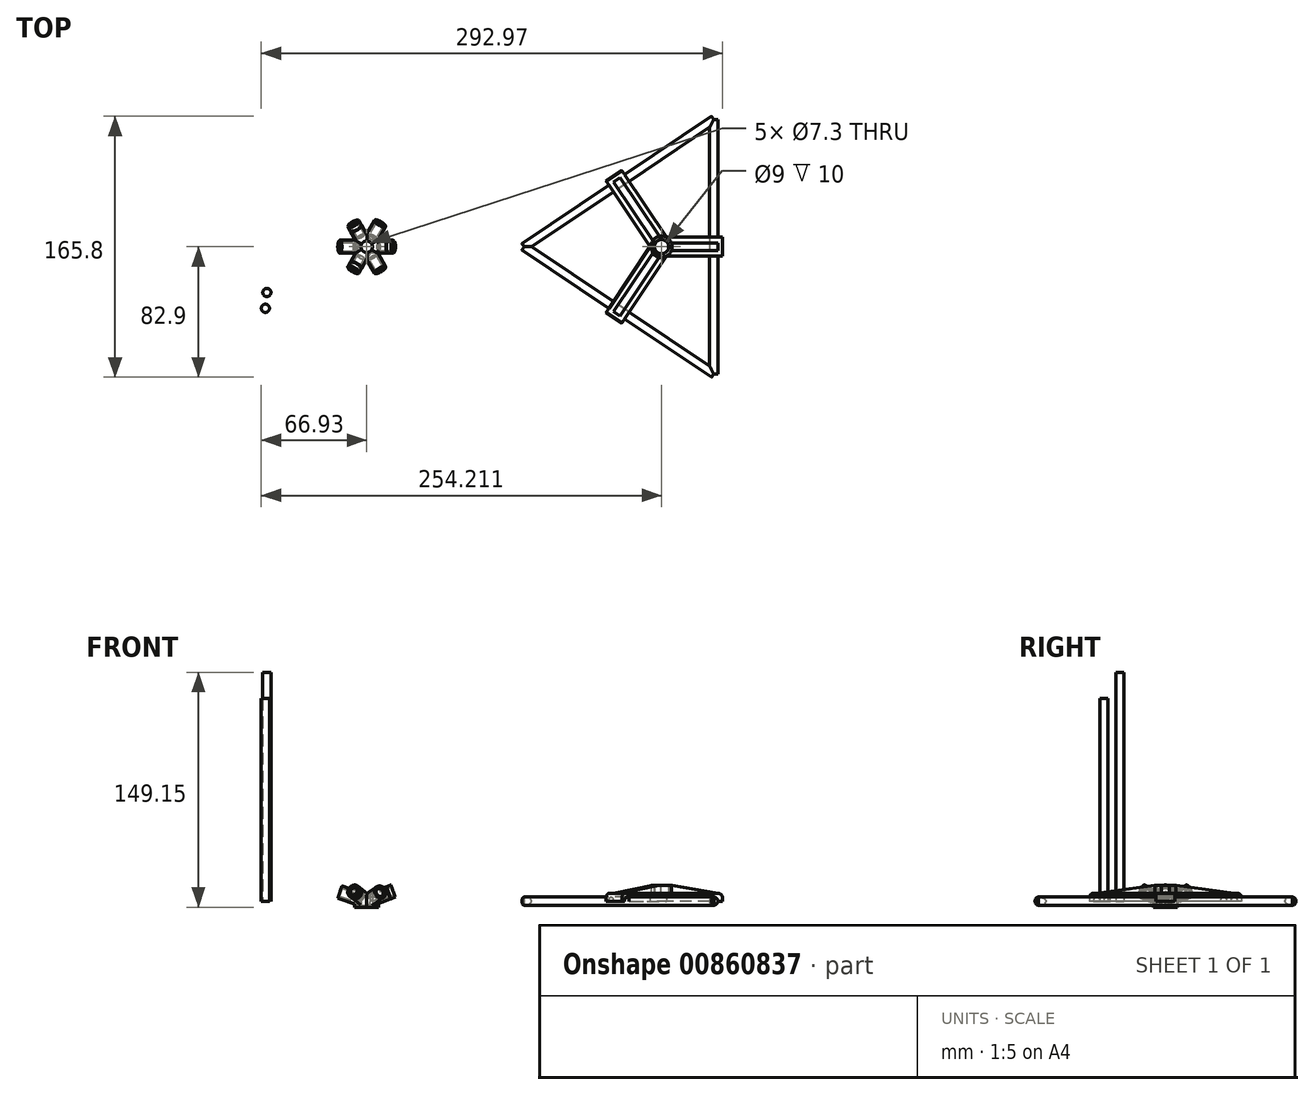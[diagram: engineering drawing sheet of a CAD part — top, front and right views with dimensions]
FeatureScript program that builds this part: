
annotation { "Feature Type Name" : "Feature", "Feature Type Description" : "" }
export const myFeature = defineFeature(function(context is Context, id is Id, definition is map)
    precondition{}
    {
        {
            assignVariable(context, id + "F0", {"name" : "espesor", "anyValue" : 1.5});
        }
        {
            assignVariable(context, id + "F1", {"name" : "longitud", "anyValue" : 18});
        }
        {
            assignVariable(context, id + "F2", {"name" : "relacion", "anyValue" : 1.11});
        }
        {
            assignVariable(context, id + "F3", {"name" : "lvarilla", "anyValue" : 145});
        }
        {
            assignVariable(context, id + "F4", {"name" : "lrecortada", "anyValue" : getVariable(context, 'lvarilla') - 2 * (getVariable(context, 'longitud') * 1.8 / 4)});
        }
        {
            assignVariable(context, id + "F5", {"name" : "lrecortadalarga", "anyValue" : (getVariable(context, 'lvarilla') * getVariable(context, 'relacion') - 2 * (getVariable(context, 'longitud') * 1.8 / 4))});
        }
        {
            var Q0;
            Q0=qCreatedBy(makeId("Front.planeOp"),FACE);
            var sketch = newSketch(context, id + "F6", { "sketchPlane" : qUnion([Q0])});
            skLineSegment(sketch, "E0", {"start": v(0, 0) * mm, "end": v(16.82, 6.42) * mm, "construction": true});
            skLineSegment(sketch, "E1", {"start": v(0, 0) * mm, "end": v(1.46, -3.83) * mm});
            skLineSegment(sketch, "E2", {"start": v(16.82, 6.42) * mm, "end": v(18.28, 2.6) * mm});
            skLineSegment(sketch, "E3", {"start": v(1.46, -3.83) * mm, "end": v(15.1, 1.38) * mm});
            skLineSegment(sketch, "E4", {"start": v(17.74, 4) * mm, "end": v(8.5, 0.46) * mm});
            skLineSegment(sketch, "E5", {"start": v(8.5, 0.46) * mm, "end": v(7.57, 2.9) * mm});
            skLineSegment(sketch, "E6", {"start": v(7.57, 2.9) * mm, "end": v(0, 0) * mm});
            skLineSegment(sketch, "E7", {"start": v(0, 0) * mm, "end": v(0, 41.35) * mm, "construction": true});
            skLineSegment(sketch, "E8", {"start": v(1.46, -3.83) * mm, "end": v(0, -3.83) * mm, "construction": true});
            skLineSegment(sketch, "E9", {"start": v(7.57, 2.9) * mm, "end": v(7.57, -3.83) * mm, "construction": true});
            skLineSegment(sketch, "E10", {"start": v(7.57, -3.83) * mm, "end": v(1.46, -3.83) * mm, "construction": true});
            skLineSegment(sketch, "E11", {"start": v(0, -3.83) * mm, "end": v(7.57, -3.83) * mm});
            skLineSegment(sketch, "E12", {"start": v(7.57, -3.83) * mm, "end": v(7.57, 2.9) * mm});
            skLineSegment(sketch, "E13", {"start": v(0, 2.9) * mm, "end": v(7.57, 2.9) * mm});
            skLineSegment(sketch, "E14", {"start": v(0, 2.9) * mm, "end": v(0, -3.83) * mm});
            skLineSegment(sketch, "E15", {"start": v(15.48, 1.52) * mm, "end": v(15.44, 1.62) * mm});
            skLineSegment(sketch, "E16", {"start": v(15.44, 1.62) * mm, "end": v(15.07, 1.47) * mm});
            skLineSegment(sketch, "E17", {"start": v(15.07, 1.47) * mm, "end": v(15.1, 1.38) * mm});
            skLineSegment(sketch, "E18.trimOffspring", {"start": v(15.48, 1.52) * mm, "end": v(18.28, 2.6) * mm});
            skSolve(sketch);
        }
        {
            var Q0;
            Q0=qCreatedBy(makeId("Front.planeOp"),FACE);
            var sketch = newSketch(context, id + "F7", { "sketchPlane" : qUnion([Q0])});
            skLineSegment(sketch, "E19", {"start": v(0, 0) * mm, "end": v(0, 45.08) * mm, "construction": true});
            skLineSegment(sketch, "E20.MirrorCS", {"start": v(-8.5, 0.13) * mm, "end": v(-7.67, 2.6) * mm});
            skLineSegment(sketch, "E21.MirrorCS", {"start": v(-17.05, 5.77) * mm, "end": v(-18.36, 1.88) * mm});
            skLineSegment(sketch, "E22.MirrorCS", {"start": v(-7.67, 2.6) * mm, "end": v(0, 0) * mm});
            skLineSegment(sketch, "E23.MirrorCS", {"start": v(0, 0) * mm, "end": v(-17.05, 5.77) * mm, "construction": true});
            skLineSegment(sketch, "E24.MirrorCS", {"start": v(0, 2.6) * mm, "end": v(-7.67, 2.6) * mm});
            skLineSegment(sketch, "E25.MirrorCS", {"start": v(-17.88, 3.3) * mm, "end": v(-8.5, 0.13) * mm});
            skLineSegment(sketch, "E26", {"start": v(-18.36, 1.88) * mm, "end": v(-1.31, -3.88) * mm});
            skLineSegment(sketch, "E27", {"start": v(0, 0) * mm, "end": v(-1.31, -3.88) * mm});
            skLineSegment(sketch, "E28", {"start": v(-1.31, -3.88) * mm, "end": v(-7.67, -3.88) * mm});
            skLineSegment(sketch, "E29", {"start": v(-1.31, -3.88) * mm, "end": v(0, -3.88) * mm});
            skLineSegment(sketch, "E30", {"start": v(0, -3.88) * mm, "end": v(0, 2.6) * mm});
            skLineSegment(sketch, "E31", {"start": v(-7.67, 2.6) * mm, "end": v(-7.67, -3.88) * mm});
            skSolve(sketch);
        }
        {
            var Q0;
            {var subQ1=sQuery(id+"F6.wireOp",EDGE,"E4");Q0=makeQuery(id+"F6.imprint","IMPRINT",FACE,{"disambiguationData":[TD([[makeQuery(id+"F6.imprint","IMPRINT",EDGE,{"derivedFrom":subQ1}),1.0]])]});}
            var Q1;
            {var subQ0=sQuery(id+"F6.wireOp",EDGE,"E1");Q1=makeQuery(id+"F6.imprint","IMPRINT",FACE,{"disambiguationData":[TD([[makeQuery(id+"F6.imprint","IMPRINT",EDGE,{"derivedFrom":subQ0}),1.0]])]});}
            var Q2;
            Q2=sQuery(id+"F6.wireOp",EDGE,"E0");
            revolve(context, id + "F8", {"surfaceOperationType" : NewSurfaceOperationType.NEW, "entities" : qUnion([Q0, Q1]), "axis" : qUnion([Q2]), "revolveType" : RevolveType.FULL});
        }
        {
            var Q0;
            {var subQ5=sQuery(id+"F7.wireOp",EDGE,"E20.MirrorCS");Q0=makeQuery(id+"F7.imprint","IMPRINT",FACE,{"disambiguationData":[TD([[makeQuery(id+"F7.imprint","IMPRINT",EDGE,{"derivedFrom":subQ5}),-1.0]])]});}
            var Q1;
            {var subQ0=sQuery(id+"F7.wireOp",EDGE,"E22.MirrorCS");Q1=makeQuery(id+"F7.imprint","IMPRINT",FACE,{"disambiguationData":[TD([[makeQuery(id+"F7.imprint","IMPRINT",EDGE,{"derivedFrom":subQ0}),-1.0]])]});}
            var Q2;
            Q2=sQuery(id+"F7.wireOp",EDGE,"E23.MirrorCS");
            revolve(context, id + "F9", {"surfaceOperationType" : NewSurfaceOperationType.NEW, "entities" : qUnion([Q0, Q1]), "axis" : qUnion([Q2]), "revolveType" : RevolveType.FULL});
        }
        {
            var Q0;
            Q0=makeQuery(id+"F8.opRevolve","SWEPT_BODY",BODY,{"disambiguationData":[OSD([sQuery(id+"F6.wireOp",EDGE,"E1"),sQuery(id+"F6.wireOp",EDGE,"E2"),sQuery(id+"F6.wireOp",EDGE,"E3"),sQuery(id+"F6.wireOp",EDGE,"E4"),sQuery(id+"F6.wireOp",EDGE,"E5"),sQuery(id+"F6.wireOp",EDGE,"E6")])]});
            var Q1;
            Q1=sQuery(id+"F6.wireOp",EDGE,"E7");
            circularPattern(context, id + "F10", {"operationType" : NewBodyOperationType.ADD, "entities" : qUnion([Q0]), "axis" : qUnion([Q1]), "angle" : 360 * degree, "instanceCount" : 3, "equalSpace" : true});
        }
        {
            var Q0;
            Q0=makeQuery(id+"FgpRCOrkwi8NXZ9_2.boolean.opBoolean","SPLIT",BODY,{"disambiguationData":[OD(1.0)],"derivedFrom":makeQuery(id+"F9.opRevolve","SWEPT_BODY",BODY,{"disambiguationData":[OSD([sQuery(id+"F7.wireOp",EDGE,"E20.MirrorCS"),sQuery(id+"F7.wireOp",EDGE,"E21.MirrorCS"),sQuery(id+"F7.wireOp",EDGE,"E22.MirrorCS"),sQuery(id+"F7.wireOp",EDGE,"E25.MirrorCS"),sQuery(id+"F7.wireOp",EDGE,"E26"),sQuery(id+"F7.wireOp",EDGE,"E27")])]})});
            var Q1;
            Q1=sQuery(id+"F7.wireOp",EDGE,"E19");
            circularPattern(context, id + "F11", {"entities" : qUnion([Q0]), "axis" : qUnion([Q1]), "angle" : 360 * degree, "instanceCount" : 3, "equalSpace" : true});
        }
        {
            var Q0;
            {var subQ0=sQuery(id+"F6.wireOp",EDGE,"E1");Q0=makeQuery(id+"F6.imprint","IMPRINT",FACE,{"disambiguationData":[TD([[makeQuery(id+"F6.imprint","IMPRINT",EDGE,{"derivedFrom":subQ0}),-1.0]])]});}
            var Q1;
            {var subQ0=sQuery(id+"F6.wireOp",EDGE,"E1");Q1=makeQuery(id+"F6.imprint","IMPRINT",FACE,{"disambiguationData":[TD([[makeQuery(id+"F6.imprint","IMPRINT",EDGE,{"derivedFrom":subQ0}),1.0]])]});}
            var Q2;
            {var subQ0=sQuery(id+"F6.wireOp",EDGE,"E11");var subQ3=sQuery(id+"F6.wireOp",EDGE,"E12");var subQ5=makeQuery(id+"F6.imprint","INTERSECT",VERTEX,{"derivedFrom":[subQ0,subQ3]});Q2=makeQuery(id+"F6.imprint","IMPRINT",FACE,{"disambiguationData":[TD([[makeQuery(id+"F6.imprint","IMPRINT",EDGE,{"disambiguationData":[TD([[subQ5,-1.0]])],"derivedFrom":subQ3}),1.0]])]});}
            var Q3;
            {var subQ0=sQuery(id+"F6.wireOp",EDGE,"E6");Q3=makeQuery(id+"F6.imprint","IMPRINT",FACE,{"disambiguationData":[TD([[makeQuery(id+"F6.imprint","IMPRINT",EDGE,{"derivedFrom":subQ0}),-1.0]])]});}
            var Q4;
            Q4=sQuery(id+"F6.wireOp",EDGE,"E13");
            var Q5;
            Q5=sQuery(id+"F6.wireOp",EDGE,"E14");
            var Q6;
            Q6=sQuery(id+"F6.wireOp",EDGE,"E7");
            revolve(context, id + "F12", {"surfaceOperationType" : NewSurfaceOperationType.NEW, "entities" : qUnion([Q0, Q1, Q2, Q3]), "surfaceEntities" : qUnion([Q4, Q5]), "axis" : qUnion([Q6]), "revolveType" : RevolveType.FULL});
        }
        {
            var Q0;
            {var subQ0=sQuery(id+"F7.wireOp",EDGE,"E22.MirrorCS");Q0=makeQuery(id+"F7.imprint","IMPRINT",FACE,{"disambiguationData":[TD([[makeQuery(id+"F7.imprint","IMPRINT",EDGE,{"derivedFrom":subQ0}),1.0]])]});}
            var Q1;
            {var subQ0=sQuery(id+"F7.wireOp",EDGE,"E22.MirrorCS");Q1=makeQuery(id+"F7.imprint","IMPRINT",FACE,{"disambiguationData":[TD([[makeQuery(id+"F7.imprint","IMPRINT",EDGE,{"derivedFrom":subQ0}),-1.0]])]});}
            var Q2;
            {var subQ0=sQuery(id+"F7.wireOp",EDGE,"E27");Q2=makeQuery(id+"F7.imprint","IMPRINT",FACE,{"disambiguationData":[TD([[makeQuery(id+"F7.imprint","IMPRINT",EDGE,{"derivedFrom":subQ0}),1.0]])]});}
            var Q3;
            {var subQ0=sQuery(id+"F7.wireOp",EDGE,"E28");Q3=makeQuery(id+"F7.imprint","IMPRINT",FACE,{"disambiguationData":[TD([[makeQuery(id+"F7.imprint","IMPRINT",EDGE,{"derivedFrom":subQ0}),-1.0]])]});}
            var Q4;
            Q4=sQuery(id+"F7.wireOp",EDGE,"E19");
            revolve(context, id + "F13", {"surfaceOperationType" : NewSurfaceOperationType.NEW, "entities" : qUnion([Q0, Q1, Q2, Q3]), "axis" : qUnion([Q4]), "revolveType" : RevolveType.FULL});
        }
        {
            var Q0;
            Q0=makeQuery(id+"F10.opPattern","COPY",EDGE,{"derivedFrom":makeQuery(id+"F8.opRevolve","SWEPT_EDGE",EDGE,{"disambiguationData":[OSD([sQuery(id+"F6.wireOp",EDGE,"E2"),sQuery(id+"F6.wireOp",EDGE,"E4")])]}),"instanceName":"5"});
            var Q1;
            Q1=makeQuery(id+"F10.opPattern","COPY",EDGE,{"derivedFrom":makeQuery(id+"F8.opRevolve","SWEPT_EDGE",EDGE,{"disambiguationData":[OSD([sQuery(id+"F6.wireOp",EDGE,"E2"),sQuery(id+"F6.wireOp",EDGE,"E4")])]}),"instanceName":"4"});
            var Q2;
            Q2=makeQuery(id+"F8.opRevolve","SWEPT_EDGE",EDGE,{"disambiguationData":[OSD([sQuery(id+"F6.wireOp",EDGE,"E2"),sQuery(id+"F6.wireOp",EDGE,"E4")])]});
            var Q3;
            Q3=makeQuery(id+"F10.opPattern","COPY",EDGE,{"derivedFrom":makeQuery(id+"F8.opRevolve","SWEPT_EDGE",EDGE,{"disambiguationData":[OSD([sQuery(id+"F6.wireOp",EDGE,"E2"),sQuery(id+"F6.wireOp",EDGE,"E4")])]}),"instanceName":"1"});
            var Q4;
            Q4=makeQuery(id+"F10.opPattern","COPY",EDGE,{"derivedFrom":makeQuery(id+"F8.opRevolve","SWEPT_EDGE",EDGE,{"disambiguationData":[OSD([sQuery(id+"F6.wireOp",EDGE,"E2"),sQuery(id+"F6.wireOp",EDGE,"E4")])]}),"instanceName":"2"});
            var Q5;
            Q5=makeQuery(id+"F10.opPattern","COPY",EDGE,{"derivedFrom":makeQuery(id+"F8.opRevolve","SWEPT_EDGE",EDGE,{"disambiguationData":[OSD([sQuery(id+"F6.wireOp",EDGE,"E2"),sQuery(id+"F6.wireOp",EDGE,"E4")])]}),"instanceName":"3"});
            var Q6;
            Q6=makeQuery(id+"F11.opPattern","COPY",EDGE,{"derivedFrom":makeQuery(id+"F9.opRevolve","SWEPT_EDGE",EDGE,{"disambiguationData":[OSD([sQuery(id+"F7.wireOp",EDGE,"E21.MirrorCS"),sQuery(id+"F7.wireOp",EDGE,"E25.MirrorCS")])]}),"instanceName":"2"});
            var Q7;
            Q7=makeQuery(id+"F9.opRevolve","SWEPT_EDGE",EDGE,{"disambiguationData":[OSD([sQuery(id+"F7.wireOp",EDGE,"E21.MirrorCS"),sQuery(id+"F7.wireOp",EDGE,"E25.MirrorCS")])]});
            var Q8;
            Q8=makeQuery(id+"F11.opPattern","COPY",EDGE,{"derivedFrom":makeQuery(id+"F9.opRevolve","SWEPT_EDGE",EDGE,{"disambiguationData":[OSD([sQuery(id+"F7.wireOp",EDGE,"E21.MirrorCS"),sQuery(id+"F7.wireOp",EDGE,"E25.MirrorCS")])]}),"instanceName":"1"});
            chamfer(context, id + "F14", {"entities" : qUnion([Q0, Q1, Q2, Q3, Q4, Q5, Q6, Q7, Q8]), "width" : (getVariable(context, 'espesor') / 2) * mm, "tangentPropagation" : true});
        }
        {
            var Q0;
            Q0=qCreatedBy(makeId("Top.planeOp"),FACE);
            var sketch = newSketch(context, id + "F15", { "sketchPlane" : qUnion([Q0])});
            skCircle(sketch, "E32", {"center": v(-64.33, -39.09) * mm, "radius": 2.6 * mm});
            skCircle(sketch, "E33", {"center": v(-63.38, -29.03) * mm, "radius": 2.6 * mm});
            skSolve(sketch);
        }
        {
            var Q0;
            Q0=makeQuery(id+"F15.imprint","IMPRINT",FACE,{"disambiguationData":[TD([[makeQuery(id+"F15.imprint","IMPRINT",EDGE,{"derivedFrom":sQuery(id+"F15.wireOp",EDGE,"E32")}),1.0]])]});
            extrude(context, id + "F16", {"entities" : qUnion([Q0]), "depth" : (getVariable(context, 'lrecortada')) * mm, "offsetDistance" : 25 * mm});
        }
        {
            var Q0;
            Q0=makeQuery(id+"F15.imprint","IMPRINT",FACE,{"disambiguationData":[TD([[makeQuery(id+"F15.imprint","IMPRINT",EDGE,{"derivedFrom":sQuery(id+"F15.wireOp",EDGE,"E33")}),1.0]])]});
            extrude(context, id + "F17", {"entities" : qUnion([Q0]), "depth" : (getVariable(context, 'lrecortadalarga')) * mm, "offsetDistance" : 25 * mm});
        }
        {
            var Q0;
            Q0=qCreatedBy(makeId("Top.planeOp"),FACE);
            var sketch = newSketch(context, id + "F18", { "sketchPlane" : qUnion([Q0])});
            skCircle(sketch, "E34", {"center": v(0, 0) * mm, "radius": 3.65 * mm});
            skSolve(sketch);
        }
        {
            var Q0;
            Q0=qSketchRegion(id+"F18",true);
            extrude(context, id + "F19", {"entities" : qUnion([Q0]), "operationType" : NewBodyOperationType.REMOVE, "depth" : 200 * mm, "offsetDistance" : 25 * mm, "symmetric" : true});
        }
        {
            var Q0;
            Q0=qCreatedBy(makeId("Top.planeOp"),FACE);
            var sketch = newSketch(context, id + "F20", { "sketchPlane" : qUnion([Q0])});
            skLineSegment(sketch, "E35", {"start": v(100, 0) * mm, "end": v(220.44, 80.74) * mm});
            skLineSegment(sketch, "E36", {"start": v(100, 0) * mm, "end": v(220.44, -80.74) * mm});
            skLineSegment(sketch, "E37", {"start": v(220.44, -80.74) * mm, "end": v(220.44, 80.74) * mm});
            skLineSegment(sketch, "E38", {"start": v(100, 0) * mm, "end": v(1382.5, 0) * mm, "construction": true});
            skLineSegment(sketch, "E39.0", {"start": v(98.55, 2.16) * mm, "end": v(219, 82.9) * mm});
            skLineSegment(sketch, "E40.0", {"start": v(223.04, -80.74) * mm, "end": v(223.04, 80.74) * mm});
            skLineSegment(sketch, "E41.0", {"start": v(98.55, -2.16) * mm, "end": v(219, -82.9) * mm});
            skLineSegment(sketch, "E42", {"start": v(98.55, 2.16) * mm, "end": v(100, 0) * mm});
            skLineSegment(sketch, "E43", {"start": v(98.55, -2.16) * mm, "end": v(100, 0) * mm});
            skLineSegment(sketch, "E44", {"start": v(220.44, 80.74) * mm, "end": v(219, 82.9) * mm});
            skLineSegment(sketch, "E45", {"start": v(220.44, 80.74) * mm, "end": v(223.04, 80.74) * mm});
            skLineSegment(sketch, "E46", {"start": v(223.04, -80.74) * mm, "end": v(220.44, -80.74) * mm});
            skLineSegment(sketch, "E47", {"start": v(220.44, -80.74) * mm, "end": v(219, -82.9) * mm});
            skLineSegment(sketch, "E48", {"start": v(160.22, 40.37) * mm, "end": v(183.92, 5.02) * mm, "construction": true});
            skLineSegment(sketch, "E49", {"start": v(160.22, -40.37) * mm, "end": v(183.1, -6.24) * mm, "construction": true});
            skLineSegment(sketch, "E50", {"start": v(162.09, 48.36) * mm, "end": v(190.48, 6) * mm});
            skLineSegment(sketch, "E51", {"start": v(190.48, -6) * mm, "end": v(162.09, -48.36) * mm});
            skLineSegment(sketch, "E52", {"start": v(152.12, 41.68) * mm, "end": v(180.06, 0) * mm});
            skLineSegment(sketch, "E53", {"start": v(180.06, 0) * mm, "end": v(152.12, -41.68) * mm});
            skLineSegment(sketch, "E54", {"start": v(226.04, 6) * mm, "end": v(190.48, 6) * mm});
            skLineSegment(sketch, "E55.MirrorCS", {"start": v(226.04, -6) * mm, "end": v(190.48, -6) * mm});
            skPoint(sketch, "E56.orphan", {"position": v(194.5, 0) * mm});
            skLineSegment(sketch, "E57", {"start": v(226.04, 6) * mm, "end": v(226.04, -6) * mm});
            skLineSegment(sketch, "E58", {"start": v(152.12, -41.68) * mm, "end": v(162.09, -48.36) * mm});
            skLineSegment(sketch, "E59", {"start": v(162.09, 48.36) * mm, "end": v(152.12, 41.68) * mm});
            skCircle(sketch, "E60", {"center": v(187.28, 0) * mm, "radius": 4.5 * mm});
            skCircle(sketch, "E61", {"center": v(187.28, 0) * mm, "radius": 6.75 * mm});
            skSolve(sketch);
        }
        {
            var Q0;
            Q0=makeQuery(id+"F20.imprint","IMPRINT",FACE,{"disambiguationData":[TD([[makeQuery(id+"F20.imprint","IMPRINT",EDGE,{"derivedFrom":sQuery(id+"F20.wireOp",EDGE,"E35")}),1.0]])]});
            var Q1;
            Q1=sQuery(id+"F20.wireOp",EDGE,"E35");
            revolve(context, id + "F21", {"surfaceOperationType" : NewSurfaceOperationType.NEW, "entities" : qUnion([Q0]), "axis" : qUnion([Q1]), "revolveType" : RevolveType.FULL});
        }
        {
            var Q0;
            Q0=makeQuery(id+"F20.imprint","IMPRINT",FACE,{"disambiguationData":[TD([[makeQuery(id+"F20.imprint","IMPRINT",EDGE,{"derivedFrom":sQuery(id+"F20.wireOp",EDGE,"E36")}),-1.0]])]});
            var Q1;
            Q1=sQuery(id+"F20.wireOp",EDGE,"E36");
            revolve(context, id + "F22", {"operationType" : NewBodyOperationType.ADD, "surfaceOperationType" : NewSurfaceOperationType.NEW, "entities" : qUnion([Q0]), "axis" : qUnion([Q1]), "revolveType" : RevolveType.FULL});
        }
        {
            var Q0;
            Q0=makeQuery(id+"F20.imprint","IMPRINT",FACE,{"disambiguationData":[TD([[makeQuery(id+"F20.imprint","IMPRINT",EDGE,{"derivedFrom":sQuery(id+"F20.wireOp",EDGE,"E37")}),-1.0]])]});
            var Q1;
            Q1=sQuery(id+"F20.wireOp",EDGE,"E37");
            revolve(context, id + "F23", {"operationType" : NewBodyOperationType.ADD, "surfaceOperationType" : NewSurfaceOperationType.NEW, "entities" : qUnion([Q0]), "axis" : qUnion([Q1]), "revolveType" : RevolveType.FULL});
        }
        {
            var Q0;
            {var subQ12=sQuery(id+"F20.wireOp",EDGE,"E35");var subQ14=sQuery(id+"F20.wireOp",EDGE,"E52");var subQ15=makeQuery(id+"F20.imprint","INTERSECT",VERTEX,{"derivedFrom":[subQ12,subQ14]});Q0=makeQuery(id+"F20.imprint","IMPRINT",FACE,{"disambiguationData":[TD([[makeQuery(id+"F20.imprint","IMPRINT",EDGE,{"disambiguationData":[TD([[subQ15,-1.0]])],"derivedFrom":subQ12}),-1.0]])]});}
            var Q1;
            {var subQ5=sQuery(id+"F20.wireOp",EDGE,"E58");Q1=makeQuery(id+"F20.imprint","IMPRINT",FACE,{"disambiguationData":[TD([[makeQuery(id+"F20.imprint","IMPRINT",EDGE,{"derivedFrom":subQ5}),1.0]])]});}
            var Q2;
            {var subQ5=sQuery(id+"F20.wireOp",EDGE,"E57");Q2=makeQuery(id+"F20.imprint","IMPRINT",FACE,{"disambiguationData":[TD([[makeQuery(id+"F20.imprint","IMPRINT",EDGE,{"derivedFrom":subQ5}),-1.0]])]});}
            var Q3;
            {var subQ5=sQuery(id+"F20.wireOp",EDGE,"E59");Q3=makeQuery(id+"F20.imprint","IMPRINT",FACE,{"disambiguationData":[TD([[makeQuery(id+"F20.imprint","IMPRINT",EDGE,{"derivedFrom":subQ5}),1.0]])]});}
            var Q4;
            {var subQ0=sQuery(id+"F20.wireOp",EDGE,"E53");var subQ1=sQuery(id+"F20.wireOp",EDGE,"E36");var subQ2=makeQuery(id+"F20.imprint","INTERSECT",VERTEX,{"derivedFrom":[subQ1,subQ0]});Q4=makeQuery(id+"F20.imprint","IMPRINT",FACE,{"disambiguationData":[TD([[makeQuery(id+"F20.imprint","IMPRINT",EDGE,{"disambiguationData":[TD([[subQ2,-1.0]])],"derivedFrom":subQ1}),-1.0]])]});}
            var Q5;
            {var subQ0=sQuery(id+"F20.wireOp",EDGE,"E55.MirrorCS");var subQ1=sQuery(id+"F20.wireOp",EDGE,"E37");var subQ2=makeQuery(id+"F20.imprint","INTERSECT",VERTEX,{"derivedFrom":[subQ1,subQ0]});Q5=makeQuery(id+"F20.imprint","IMPRINT",FACE,{"disambiguationData":[TD([[makeQuery(id+"F20.imprint","IMPRINT",EDGE,{"disambiguationData":[TD([[subQ2,-1.0]])],"derivedFrom":subQ1}),-1.0]])]});}
            var Q6;
            {var subQ0=sQuery(id+"F20.wireOp",EDGE,"E52");var subQ1=sQuery(id+"F20.wireOp",EDGE,"E35");var subQ2=makeQuery(id+"F20.imprint","INTERSECT",VERTEX,{"derivedFrom":[subQ1,subQ0]});Q6=makeQuery(id+"F20.imprint","IMPRINT",FACE,{"disambiguationData":[TD([[makeQuery(id+"F20.imprint","IMPRINT",EDGE,{"disambiguationData":[TD([[subQ2,-1.0]])],"derivedFrom":subQ1}),1.0]])]});}
            var Q7;
            Q7=makeQuery(id+"F20.imprint","IMPRINT",FACE,{"disambiguationData":[TD([[makeQuery(id+"F20.imprint","IMPRINT",EDGE,{"derivedFrom":sQuery(id+"F20.wireOp",EDGE,"E60")}),-1.0]])]});
            extrude(context, id + "F24", {"entities" : qUnion([Q0, Q1, Q2, Q3, Q4, Q5, Q6, Q7]), "depth" : 5 * mm, "offsetDistance" : 25 * mm});
        }
        {
            var Q0;
            Q0=makeQuery(id+"F20.imprint","IMPRINT",FACE,{"disambiguationData":[TD([[makeQuery(id+"F20.imprint","IMPRINT",EDGE,{"derivedFrom":sQuery(id+"F20.wireOp",EDGE,"E60")}),-1.0]])]});
            extrude(context, id + "F25", {"entities" : qUnion([Q0]), "operationType" : NewBodyOperationType.ADD, "depth" : 10 * mm, "offsetDistance" : 25 * mm});
        }
        {
            var Q0;
            Q0=makeQuery(id+"F21.opRevolve","SWEPT_BODY",BODY,{"disambiguationData":[OSD([sQuery(id+"F20.wireOp",EDGE,"E35"),sQuery(id+"F20.wireOp",EDGE,"E39.0"),sQuery(id+"F20.wireOp",EDGE,"E42"),sQuery(id+"F20.wireOp",EDGE,"E44")])]});
            var Q1;
            Q1=makeQuery(id+"F24.opExtrude","SWEPT_BODY",BODY,{"disambiguationData":[OSD([sQuery(id+"F20.wireOp",EDGE,"E50"),sQuery(id+"F20.wireOp",EDGE,"E51"),sQuery(id+"F20.wireOp",EDGE,"E52"),sQuery(id+"F20.wireOp",EDGE,"E53"),sQuery(id+"F20.wireOp",EDGE,"E54"),sQuery(id+"F20.wireOp",EDGE,"E55.MirrorCS"),sQuery(id+"F20.wireOp",EDGE,"E57"),sQuery(id+"F20.wireOp",EDGE,"E58"),sQuery(id+"F20.wireOp",EDGE,"E59"),sQuery(id+"F20.wireOp",EDGE,"E61")])]});
            booleanBodies(context, id + "F26", {"operationType" : BooleanOperationType.SUBTRACTION, "tools" : qUnion([Q0]), "targets" : qUnion([Q1]), "keepTools" : true});
        }
        {
            var Q0;
            Q0=qCreatedBy(makeId("Front.planeOp"),FACE);
            var sketch = newSketch(context, id + "F27", { "sketchPlane" : qUnion([Q0])});
            skLineSegment(sketch, "E62.0.0", {"start": v(226.04, 0) * mm, "end": v(223.04, 0) * mm});
            skArc(sketch, "E62.0.1", {"start": v(223.04, 0) * mm, "mid": v(220.44, 2.6) * mm, "end": v(217.84, 0) * mm});
            skLineSegment(sketch, "E62.0.2", {"start": v(217.84, 0) * mm, "end": v(190.48, 0) * mm});
            skLineSegment(sketch, "E62.0.3", {"start": v(190.48, 0) * mm, "end": v(190.48, 5) * mm});
            skLineSegment(sketch, "E62.0.4", {"start": v(190.48, 5) * mm, "end": v(226.04, 5) * mm});
            skLineSegment(sketch, "E62.0.5", {"start": v(226.04, 5) * mm, "end": v(226.04, 0) * mm});
            skLineSegment(sketch, "E63", {"start": v(223.04, 5) * mm, "end": v(194.03, 10) * mm});
            skLineSegment(sketch, "E64.0.0", {"start": v(180.53, 10) * mm, "end": v(194.03, 10) * mm});
            skLineSegment(sketch, "E65.0", {"start": v(182.78, 10) * mm, "end": v(191.78, 10) * mm});
            skLineSegment(sketch, "E66", {"start": v(194.03, 10) * mm, "end": v(191.78, 10) * mm});
            skLineSegment(sketch, "E67", {"start": v(191.78, 10) * mm, "end": v(191.78, 5) * mm});
            skSolve(sketch);
        }
        {
            var Q0;
            {var subQ0=sQuery(id+"F27.wireOp",EDGE,"E63");Q0=makeQuery(id+"F27.imprint","IMPRINT",FACE,{"disambiguationData":[TD([[makeQuery(id+"F27.imprint","IMPRINT",EDGE,{"derivedFrom":subQ0}),1.0]])]});}
            extrude(context, id + "F28", {"entities" : qUnion([Q0]), "operationType" : NewBodyOperationType.ADD, "depth" : 5 * mm, "offsetDistance" : 25 * mm, "symmetric" : true});
        }
        {
            var Q0;
            Q0=makeQuery(id+"F24.opExtrude","SWEPT_FACE",FACE,{"disambiguationData":[OSD([sQuery(id+"F20.wireOp",EDGE,"E52")])]});
            cPlane(context, id + "F29", {"entities" : qUnion([Q0]), "cplaneType" : CPlaneType.OFFSET, "offset" : 6 * mm, "oppositeDirection" : true, "width" : 150 * mm, "height" : 150 * mm});
        }
        {
            var Q0;
            Q0=qCreatedBy(id+"F29.planeOp",FACE);
            var sketch = newSketch(context, id + "F30", { "sketchPlane" : qUnion([Q0])});
            skArc(sketch, "E68.0.0", {"start": v(58.28, 0) * mm, "mid": v(55.68, 2.6) * mm, "end": v(53.08, 0) * mm});
            skLineSegment(sketch, "E68.0.1", {"start": v(53.08, 0) * mm, "end": v(50.08, 0) * mm});
            skLineSegment(sketch, "E68.0.2", {"start": v(50.08, 0) * mm, "end": v(50.08, 5) * mm});
            skLineSegment(sketch, "E68.0.3", {"start": v(50.08, 5) * mm, "end": v(101.08, 5) * mm});
            skLineSegment(sketch, "E68.0.4", {"start": v(101.08, 5) * mm, "end": v(101.08, 0) * mm});
            skLineSegment(sketch, "E68.0.5", {"start": v(101.08, 0) * mm, "end": v(58.28, 0) * mm});
            skLineSegment(sketch, "E69", {"start": v(53.08, 5) * mm, "end": v(97.53, 10) * mm});
            skLineSegment(sketch, "E70", {"start": v(97.53, 5) * mm, "end": v(84.63, 5) * mm});
            skLineSegment(sketch, "E71", {"start": v(97.53, 10) * mm, "end": v(99.78, 10) * mm});
            skLineSegment(sketch, "E72", {"start": v(99.78, 5) * mm, "end": v(99.78, 10) * mm});
            skSolve(sketch);
        }
        {
            var Q0;
            {var subQ0=sQuery(id+"F30.wireOp",EDGE,"E69");Q0=makeQuery(id+"F30.imprint","IMPRINT",FACE,{"disambiguationData":[TD([[makeQuery(id+"F30.imprint","IMPRINT",EDGE,{"derivedFrom":subQ0}),-1.0]])]});}
            extrude(context, id + "F31", {"entities" : qUnion([Q0]), "depth" : 5 * mm, "offsetDistance" : 25 * mm, "symmetric" : true});
        }
        {
            var Q0;
            Q0=makeQuery(id+"F31.opExtrude","SWEPT_BODY",BODY,{"disambiguationData":[OSD([sQuery(id+"F30.wireOp",EDGE,"E68.0.3"),sQuery(id+"F30.wireOp",EDGE,"E69"),sQuery(id+"F30.wireOp",EDGE,"E71"),sQuery(id+"F30.wireOp",EDGE,"E72")])]});
            var Q1;
            Q1=sQuery(id+"F20.wireOp",EDGE,"E60");
            transform(context, id + "F32", {"entities" : qUnion([Q0]), "transformType" : TransformType.ROTATION, "transformAxis" : qUnion([Q1]), "angle" : 112.33 * degree, "makeCopy" : true});
        }
        {
            var Q0;
            Q0=makeQuery(id+"F24.opExtrude","CAP_EDGE",EDGE,{"disambiguationData":[OSD([sQuery(id+"F20.wireOp",EDGE,"E57")])],"isStart":false});
            var Q1;
            Q1=makeQuery(id+"F24.opExtrude","CAP_EDGE",EDGE,{"disambiguationData":[OSD([sQuery(id+"F20.wireOp",EDGE,"E59")])],"isStart":false});
            var Q2;
            Q2=makeQuery(id+"F24.opExtrude","CAP_EDGE",EDGE,{"disambiguationData":[OSD([sQuery(id+"F20.wireOp",EDGE,"E58")])],"isStart":false});
            fillet(context, id + "F33", {"entities" : qUnion([Q0, Q1, Q2]), "radius" : 3 * mm, "tangentPropagation" : true, "allowEdgeOverflow" : false});
        }
    });
